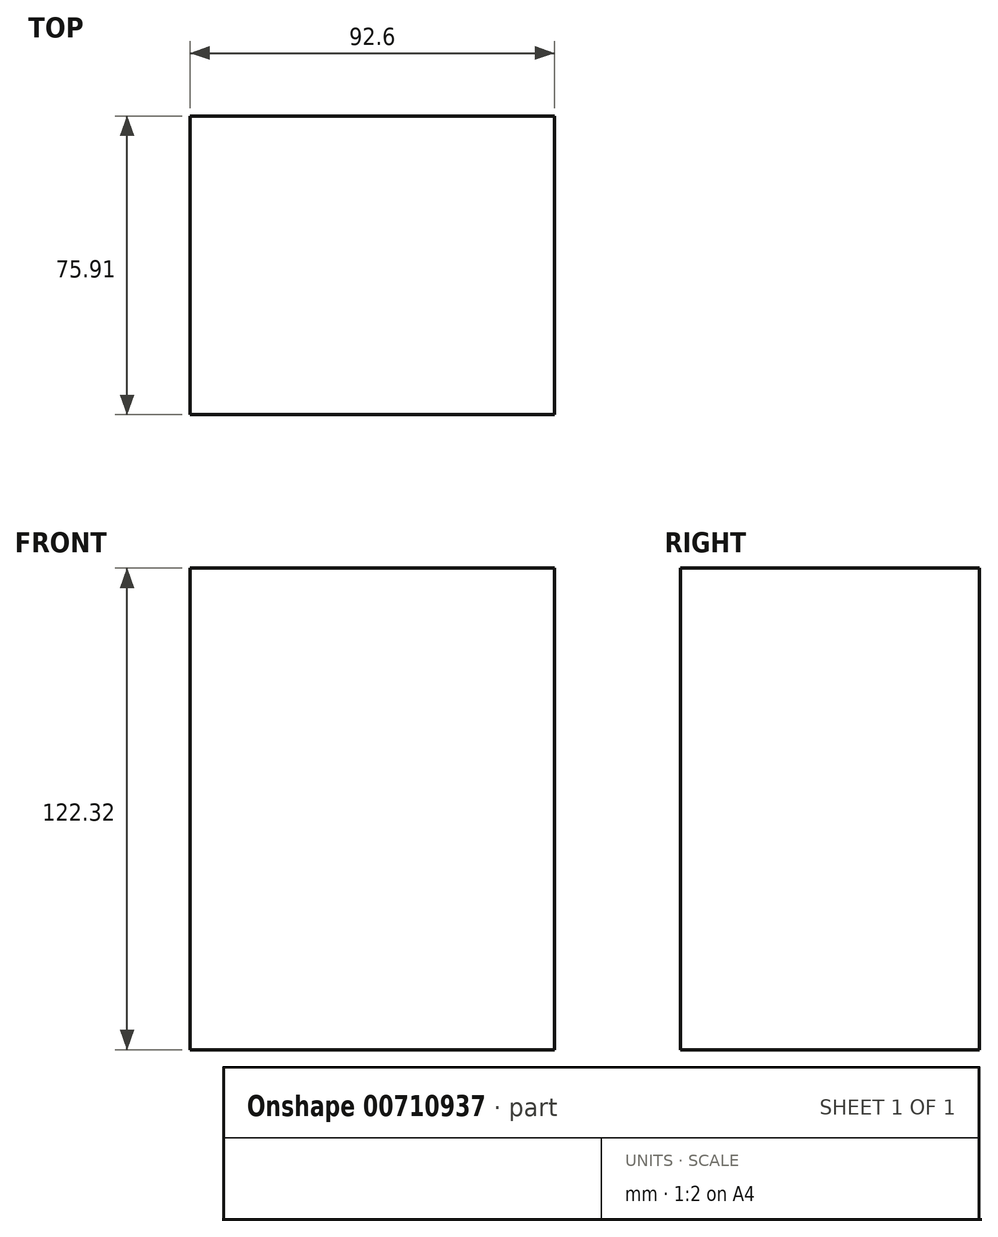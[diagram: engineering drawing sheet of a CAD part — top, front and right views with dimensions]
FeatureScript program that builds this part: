
annotation { "Feature Type Name" : "Feature", "Feature Type Description" : "" }
export const myFeature = defineFeature(function(context is Context, id is Id, definition is map)
    precondition{}
    {
        {
            var Q0;
            Q0=qCreatedBy(makeId("Front.planeOp"),FACE);
            var sketch = newSketch(context, id + "F0", { "sketchPlane" : qUnion([Q0])});
            skLineSegment(sketch, "E0.bottom", {"start": v(0, 0) * mm, "end": v(92.6, 0) * mm});
            skLineSegment(sketch, "E0.top", {"start": v(0, 122.32) * mm, "end": v(92.6, 122.32) * mm});
            skLineSegment(sketch, "E0.left", {"start": v(0, 0) * mm, "end": v(0, 122.32) * mm});
            skLineSegment(sketch, "E0.right", {"start": v(92.6, 0) * mm, "end": v(92.6, 122.32) * mm});
            skSolve(sketch);
        }
        {
            var Q0;
            Q0=makeQuery(id+"F0.imprint","IMPRINT",FACE,{"disambiguationData":[TD([[makeQuery(id+"F0.imprint","IMPRINT",EDGE,{"derivedFrom":sQuery(id+"F0.wireOp",EDGE,"E0.bottom")}),1.0]])]});
            extrude(context, id + "F1", {"entities" : qUnion([Q0]), "depth" : 75.9 * mm, "offsetDistance" : 25.4 * mm});
        }
    });
